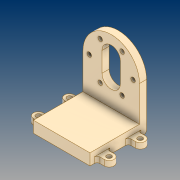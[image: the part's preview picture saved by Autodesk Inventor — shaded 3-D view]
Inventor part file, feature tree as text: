
AUTODESK INVENTOR PART (.ipt)
format: ipt  version: 2021 (Build 250183000, 183)  size: 231,936 bytes
history: native  units: mm
features: extrude x4, sketch x4, projected_geometry x3, fillet x2, plane x2, mirror x2
ambient origin geometry x8: Origin, YZ Plane, XZ Plane, XY Plane, X Axis, Y Axis, Z Axis, Center Point
bodies: Solid1 (feature_tree)
feature tree (17):
  extrude  "Extrusion1"  Depth=40.0mm
  extrude  "Extrusion2"  Depth=60.0mm TaperAngle=360.0deg
  extrude  "Extrusion3"  Depth=5.0mm
  fillet  "Fillet1"  Radius=5.0mm
  extrude  "Extrusion4"  Depth=2.0mm
  plane  "Work Plane1"
  plane  "Work Plane2"
  mirror  "Mirror2"
  mirror  "Mirror3"
  fillet  "Fillet4"  [1 undecoded]
  sketch  "Sketch1"  dims[d0=40.0mm d1=15.55mm]
  sketch  "Sketch2"  dims[d3=33.0mm d4=60.0mm d6=360.0deg]
  projected_geometry  "Projected Loop1"
  sketch  "Sketch3"  dims[d8=6.5mm d9=14.0mm d10=5.0mm d11=0.0mm]
  projected_geometry  "Projected Loop2"
  sketch  "Sketch4"  dims[d12=31.0mm d13=3.2mm d14=30.0deg d15=60.0mm d17=360.0deg d19=5.0mm d20=0.0mm d21=40.0mm d22=8.0mm d23=0.0mm d24=2.0mm d26=7.0mm d27=5.0mm d28=4.0mm d29=3.5mm d30=4.0mm d31=0.0mm d33=-2.0mm d34=2.0mm]
  projected_geometry  "Projected Loop3"
note: 1 required parameter value undecoded (feature->parameter linkage not recoverable at this tier; creation-order binding heuristic only, values carry confidence <= 0.55)
